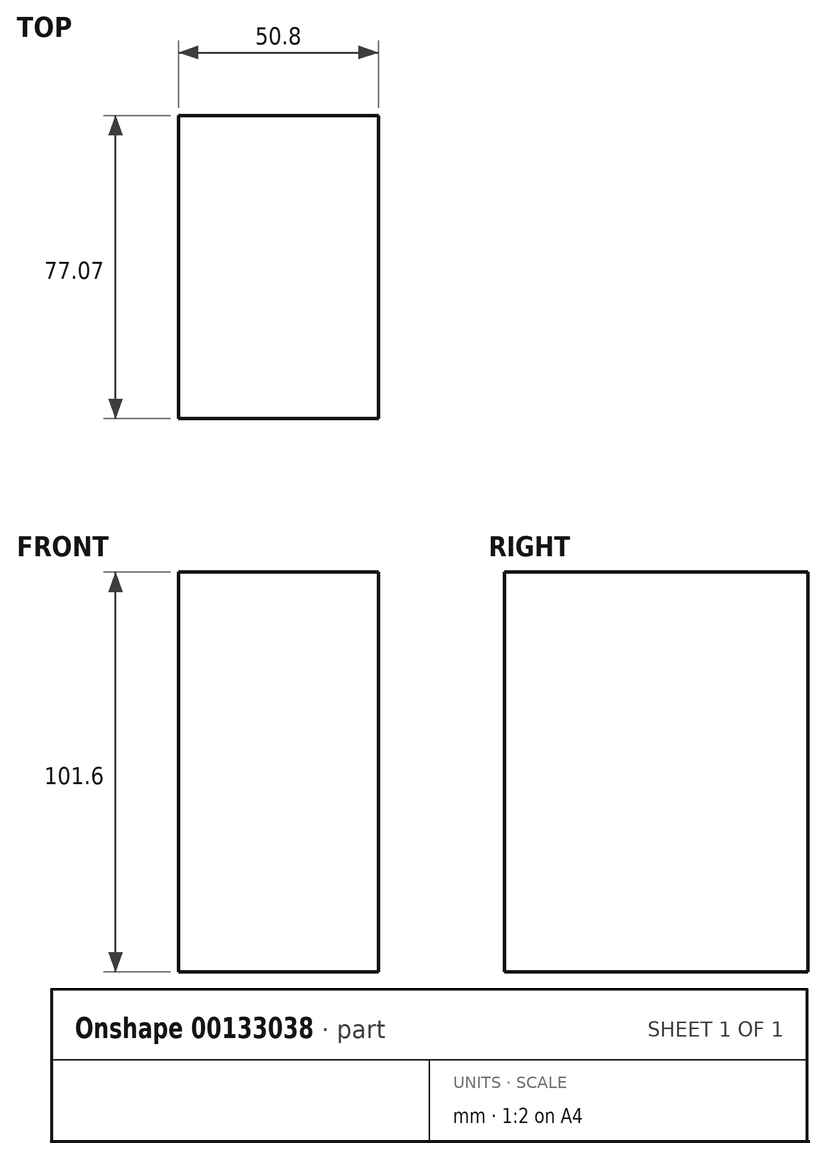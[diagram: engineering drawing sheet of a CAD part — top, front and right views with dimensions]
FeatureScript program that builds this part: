
annotation { "Feature Type Name" : "Feature", "Feature Type Description" : "" }
export const myFeature = defineFeature(function(context is Context, id is Id, definition is map)
    precondition{}
    {
        {
            var Q0;
            Q0=qCreatedBy(makeId("Front.planeOp"),FACE);
            var sketch = newSketch(context, id + "F0", { "sketchPlane" : qUnion([Q0])});
            skLineSegment(sketch, "E0.bottom", {"start": v(-25.4, 50.8) * mm, "end": v(25.4, 50.8) * mm});
            skLineSegment(sketch, "E0.top", {"start": v(-25.4, -50.8) * mm, "end": v(25.4, -50.8) * mm});
            skLineSegment(sketch, "E0.left", {"start": v(-25.4, 50.8) * mm, "end": v(-25.4, -50.8) * mm});
            skLineSegment(sketch, "E0.right", {"start": v(25.4, 50.8) * mm, "end": v(25.4, -50.8) * mm});
            skPoint(sketch, "E0.middle", {"position": v(0, 0) * mm});
            skSolve(sketch);
        }
        {
            var Q0;
            Q0 = qSketchRegion(id + "F0", true);
            var Q1;
            Q1=makeQuery(id+"F0.imprint","IMPRINT",FACE,{"disambiguationData":[TD([[makeQuery(id+"F0.imprint","IMPRINT",EDGE,{"derivedFrom":sQuery(id+"F0.wireOp",EDGE,"E0.bottom")}),-1.0]])]});
            extrude(context, id + "F1", {"entities" : qUnion([Q0, Q1]), "depth" : 77.07 * mm});
        }
    });
